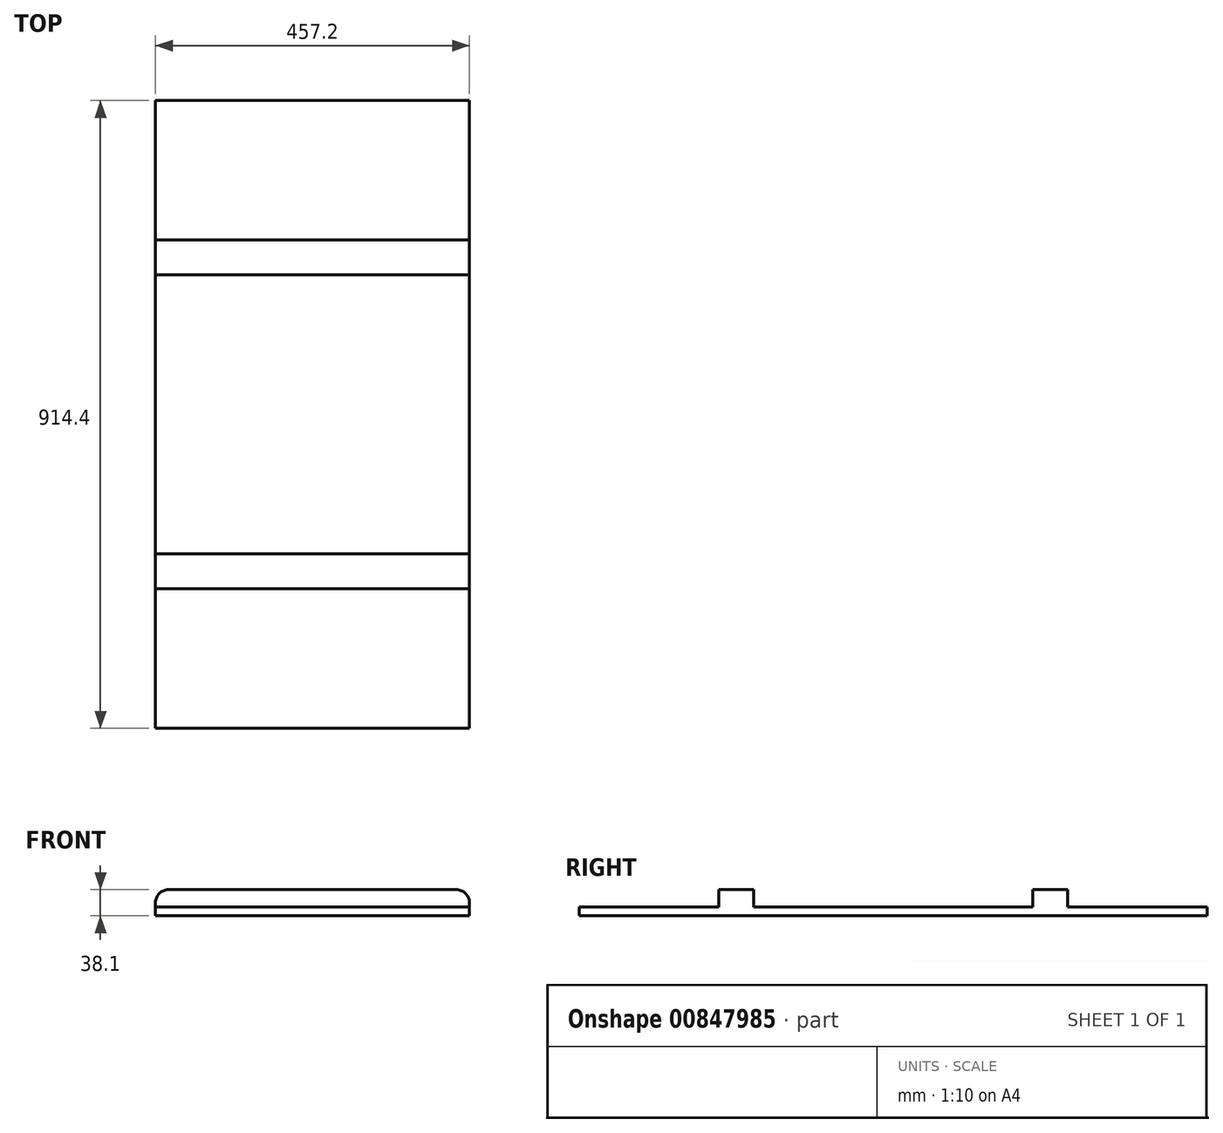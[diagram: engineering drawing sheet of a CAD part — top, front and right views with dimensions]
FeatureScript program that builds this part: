
annotation { "Feature Type Name" : "Feature", "Feature Type Description" : "" }
export const myFeature = defineFeature(function(context is Context, id is Id, definition is map)
    precondition{}
    {
        {
            var Q0;
            Q0=qCreatedBy(makeId("Top.planeOp"),FACE);
            var sketch = newSketch(context, id + "F0", { "sketchPlane" : qUnion([Q0])});
            skLineSegment(sketch, "E0.bottom", {"start": v(228.6, 457.2) * mm, "end": v(-228.6, 457.2) * mm});
            skLineSegment(sketch, "E0.top", {"start": v(228.6, -457.2) * mm, "end": v(-228.6, -457.2) * mm});
            skLineSegment(sketch, "E0.left", {"start": v(228.6, 457.2) * mm, "end": v(228.6, -457.2) * mm});
            skLineSegment(sketch, "E0.right", {"start": v(-228.6, 457.2) * mm, "end": v(-228.6, -457.2) * mm});
            skPoint(sketch, "E0.middle", {"position": v(0, 0) * mm});
            skSolve(sketch);
        }
        {
            var Q0;
            Q0=makeQuery(id+"F0.imprint","IMPRINT",FACE,{"disambiguationData":[TD([[makeQuery(id+"F0.imprint","IMPRINT",EDGE,{"derivedFrom":sQuery(id+"F0.wireOp",EDGE,"E0.bottom")}),1.0]])]});
            extrude(context, id + "F1", {"entities" : qUnion([Q0]), "depth" : 12.7 * mm, "offsetDistance" : 25.4 * mm});
        }
        {
            var Q0;
            Q0=makeQuery(id+"F1.opExtrude","CAP_FACE",FACE,{"disambiguationData":[OSD([sQuery(id+"F0.wireOp",EDGE,"E0.bottom"),sQuery(id+"F0.wireOp",EDGE,"E0.top"),sQuery(id+"F0.wireOp",EDGE,"E0.left"),sQuery(id+"F0.wireOp",EDGE,"E0.right")])],"isStart":false});
            var sketch = newSketch(context, id + "F2", { "sketchPlane" : qUnion([Q0])});
            skLineSegment(sketch, "E1.bottom", {"start": v(228.6, 254) * mm, "end": v(-228.6, 254) * mm});
            skLineSegment(sketch, "E1.top", {"start": v(228.6, 203.2) * mm, "end": v(-228.6, 203.2) * mm});
            skLineSegment(sketch, "E1.left", {"start": v(228.6, 254) * mm, "end": v(228.6, 203.2) * mm});
            skLineSegment(sketch, "E1.right", {"start": v(-228.6, 254) * mm, "end": v(-228.6, 203.2) * mm});
            skLineSegment(sketch, "E2.bottom", {"start": v(228.6, -203.2) * mm, "end": v(-228.6, -203.2) * mm});
            skLineSegment(sketch, "E2.top", {"start": v(228.6, -254) * mm, "end": v(-228.6, -254) * mm});
            skLineSegment(sketch, "E2.left", {"start": v(228.6, -203.2) * mm, "end": v(228.6, -254) * mm});
            skLineSegment(sketch, "E2.right", {"start": v(-228.6, -203.2) * mm, "end": v(-228.6, -254) * mm});
            skSolve(sketch);
        }
        {
            var Q0;
            Q0=makeQuery(id+"F2.imprint","IMPRINT",FACE,{"disambiguationData":[TD([[makeQuery(id+"F2.imprint","IMPRINT",EDGE,{"derivedFrom":sQuery(id+"F2.wireOp",EDGE,"E2.bottom")}),1.0]])]});
            var Q1;
            Q1=makeQuery(id+"F2.imprint","IMPRINT",FACE,{"disambiguationData":[TD([[makeQuery(id+"F2.imprint","IMPRINT",EDGE,{"derivedFrom":sQuery(id+"F2.wireOp",EDGE,"E1.bottom")}),1.0]])]});
            extrude(context, id + "F3", {"entities" : qUnion([Q0, Q1]), "operationType" : NewBodyOperationType.ADD, "depth" : 25.4 * mm, "offsetDistance" : 25.4 * mm});
        }
        {
            var Q0;
            Q0=makeQuery(id+"F3.opExtrude","CAP_EDGE",EDGE,{"disambiguationData":[OSD([sQuery(id+"F2.wireOp",EDGE,"E2.right")])],"isStart":false});
            var Q1;
            Q1=makeQuery(id+"F3.opExtrude","CAP_EDGE",EDGE,{"disambiguationData":[OSD([sQuery(id+"F2.wireOp",EDGE,"E2.left")])],"isStart":false});
            var Q2;
            Q2=makeQuery(id+"F3.opExtrude","CAP_EDGE",EDGE,{"disambiguationData":[OSD([sQuery(id+"F2.wireOp",EDGE,"E1.left")])],"isStart":false});
            var Q3;
            Q3=makeQuery(id+"F3.opExtrude","CAP_EDGE",EDGE,{"disambiguationData":[OSD([sQuery(id+"F2.wireOp",EDGE,"E1.right")])],"isStart":false});
            fillet(context, id + "F4", {"entities" : qUnion([Q0, Q1, Q2, Q3]), "radius" : 19.05 * mm, "tangentPropagation" : true, "allowEdgeOverflow" : false});
        }
    });
